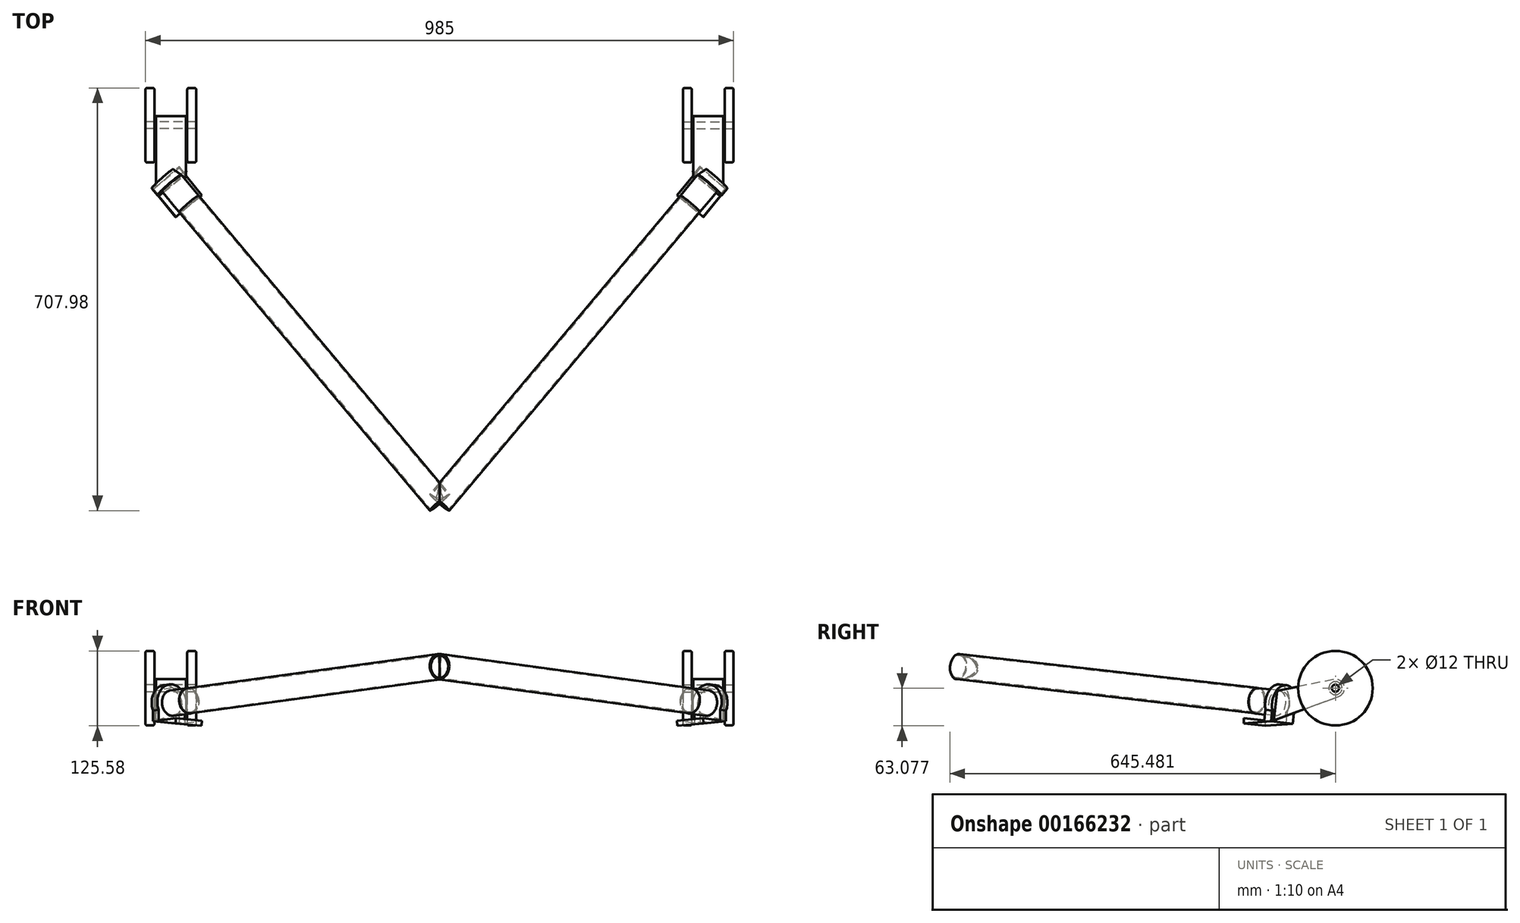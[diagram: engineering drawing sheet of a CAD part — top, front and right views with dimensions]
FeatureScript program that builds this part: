
annotation { "Feature Type Name" : "Feature", "Feature Type Description" : "" }
export const myFeature = defineFeature(function(context is Context, id is Id, definition is map)
    precondition{}
    {
        {
            var Q0;
            Q0=qCreatedBy(makeId("Top.planeOp"),FACE);
            var sketch = newSketch(context, id + "F0", { "sketchPlane" : qUnion([Q0])});
            skLineSegment(sketch, "E0", {"start": v(0, 492.45) * mm, "end": v(0, -616.45) * mm, "construction": true});
            skLineSegment(sketch, "E1", {"start": v(0, 0) * mm, "end": v(449.95, 536.23) * mm, "construction": true});
            skLineSegment(sketch, "E2", {"start": v(0, 0) * mm, "end": v(-449.95, 536.23) * mm, "construction": true});
            skSolve(sketch);
        }
        {
            var Q0;
            Q0=sQuery(id+"F0.wireOp",EDGE,"E1");
            var Q1;
            Q1=qCreatedBy(makeId("Front.planeOp"),FACE);
            cPlane(context, id + "F1", {"entities" : qUnion([Q0, Q1]), "cplaneType" : CPlaneType.LINE_ANGLE, "offset" : 25 * mm, "angle" : 0 * degree, "width" : 150 * mm, "height" : 150 * mm});
        }
        {
            var Q0;
            Q0=qCreatedBy(id+"F1.planeOp",FACE);
            var sketch = newSketch(context, id + "F2", { "sketchPlane" : qUnion([Q0])});
            skPoint(sketch, "E3.0", {"position": v(-700, 0) * mm});
            skLineSegment(sketch, "E4.0", {"start": v(0, 0) * mm, "end": v(-700, 0) * mm, "construction": true});
            skLineSegment(sketch, "E5", {"start": v(-700, 0) * mm, "end": v(0, 61.24) * mm, "construction": true});
            skSolve(sketch);
        }
        {
            var Q0;
            Q0=sQuery(id+"F2.wireOp",VERTEX,"E5.end");
            var Q1;
            Q1=sQuery(id+"F2.wireOp",EDGE,"E5");
            cPlane(context, id + "F3", {"entities" : qUnion([Q0, Q1]), "cplaneType" : CPlaneType.LINE_POINT, "offset" : 25 * mm, "width" : 150 * mm, "height" : 150 * mm});
        }
        {
            var Q0;
            Q0=qCreatedBy(id+"F3.planeOp",FACE);
            var sketch = newSketch(context, id + "F4", { "sketchPlane" : qUnion([Q0])});
            skPoint(sketch, "E6.0", {"position": v(4.45, 60.85) * mm});
            skCircle(sketch, "E7", {"center": v(4.45, 60.85) * mm, "radius": 21.3 * mm});
            skCircle(sketch, "E8.0", {"center": v(4.45, 60.85) * mm, "radius": 19.3 * mm});
            skSolve(sketch);
        }
        {
            var Q0;
            Q0 = qSketchRegion(id + "F4", true);
            extrude(context, id + "F5", {"entities" : qUnion([Q0]), "oppositeDirection" : true, "depth" : 700 * mm});
        }
        {
            var Q0;
            Q0=makeQuery(id+"F5.opExtrude","CAP_FACE",FACE,{"disambiguationData":[OSD([sQuery(id+"F4.wireOp",EDGE,"E7"),sQuery(id+"F4.wireOp",EDGE,"E8.0")])],"isStart":false});
            cPlane(context, id + "F6", {"entities" : qUnion([Q0]), "cplaneType" : CPlaneType.OFFSET, "offset" : (0.2 + 15) * mm, "width" : 150 * mm, "height" : 150 * mm});
        }
        {
            var Q0;
            Q0=qCreatedBy(id+"F6.planeOp",FACE);
            var sketch = newSketch(context, id + "F7", { "sketchPlane" : qUnion([Q0])});
            skCircle(sketch, "E9.0", {"center": v(-4.45, 60.85) * mm, "radius": 21.45 * mm});
            skArc(sketch, "E10.0", {"start": v(23.98, 47.4) * mm, "mid": v(-4.45, 92.3) * mm, "end": v(-32.88, 47.4) * mm});
            skLineSegment(sketch, "E11.top", {"start": v(-32.88, 29.4) * mm, "end": v(23.98, 29.4) * mm});
            skLineSegment(sketch, "E11.left", {"start": v(-32.88, 47.4) * mm, "end": v(-32.88, 29.4) * mm});
            skLineSegment(sketch, "E11.right", {"start": v(23.98, 47.4) * mm, "end": v(23.98, 29.4) * mm});
            skPoint(sketch, "E12", {"position": v(-4.45, 29.4) * mm});
            skSolve(sketch);
        }
        {
            var Q0;
            Q0=makeQuery(id+"F7.imprint","IMPRINT",FACE,{"disambiguationData":[TD([[makeQuery(id+"F7.imprint","IMPRINT",EDGE,{"derivedFrom":sQuery(id+"F7.wireOp",EDGE,"E9.0")}),-1.0]])]});
            var Q1;
            Q1=makeQuery(id+"F7.imprint","IMPRINT",FACE,{"disambiguationData":[TD([[makeQuery(id+"F7.imprint","IMPRINT",EDGE,{"derivedFrom":sQuery(id+"F7.wireOp",EDGE,"E9.0")}),1.0]])]});
            extrude(context, id + "F8", {"entities" : qUnion([Q0, Q1]), "oppositeDirection" : true, "depth" : 60 * mm});
        }
        {
            var Q0;
            Q0=makeQuery(id+"F8.opExtrude","CAP_FACE",FACE,{"disambiguationData":[OSD([sQuery(id+"F7.wireOp",EDGE,"E10.0"),sQuery(id+"F7.wireOp",EDGE,"E11.top"),sQuery(id+"F7.wireOp",EDGE,"E11.left"),sQuery(id+"F7.wireOp",EDGE,"E11.right")])],"isStart":false});
            var sketch = newSketch(context, id + "F9", { "sketchPlane" : qUnion([Q0])});
            skCircle(sketch, "E13.0", {"center": v(4.45, 60.85) * mm, "radius": 21.45 * mm});
            skSolve(sketch);
        }
        {
            var Q0;
            Q0=qCreatedBy(makeId("Right.planeOp"),FACE);
            cPlane(context, id + "F10", {"entities" : qUnion([Q0]), "cplaneType" : CPlaneType.OFFSET, "offset" : 475 * mm, "width" : 150 * mm, "height" : 150 * mm});
        }
        {
            var Q0;
            Q0=qCreatedBy(id+"F10.planeOp",FACE);
            var sketch = newSketch(context, id + "F11", { "sketchPlane" : qUnion([Q0])});
            skLineSegment(sketch, "E14.0", {"start": v(526.18, -12.39) * mm, "end": v(524.13, -30.27) * mm});
            skLineSegment(sketch, "E15", {"start": v(524.13, -30.27) * mm, "end": v(636.87, 11.03) * mm});
            skLineSegment(sketch, "E16", {"start": v(628.72, 39.82) * mm, "end": v(529.85, 19.73) * mm});
            skPoint(sketch, "E17.visualSharp", {"position": v(823.37, 79.36) * mm});
            skArc(sketch, "E17.filletArc", {"start": v(636.87, 11.03) * mm, "mid": v(646.14, 29.2) * mm, "end": v(628.72, 39.82) * mm});
            skCircle(sketch, "E18", {"center": v(631.71, 25.12) * mm, "radius": 6 * mm});
            skLineSegment(sketch, "E19", {"start": v(526.18, -12.39) * mm, "end": v(529.85, 19.73) * mm});
            skSolve(sketch);
        }
        {
            var Q0;
            Q0 = qSketchRegion(id + "F11", true);
            var Q1;
            {var subQ0=sQuery(id+"F7.wireOp",EDGE,"E9.0");Q1=makeQuery(id+"F5WumAtOTFpTSAU_2.boolean.opBoolean","MERGE",FACE,{"derivedFrom":[makeQuery(id+"F8.opExtrude","CAP_FACE",FACE,{"disambiguationData":[OSD([subQ0,sQuery(id+"F7.wireOp",EDGE,"E10.0"),sQuery(id+"F7.wireOp",EDGE,"E11.top"),sQuery(id+"F7.wireOp",EDGE,"E11.left"),sQuery(id+"F7.wireOp",EDGE,"E11.right")])],"isStart":true}),makeQuery(id+"F5WumAtOTFpTSAU_2.opExtrude","CAP_FACE",FACE,{"disambiguationData":[OSD([subQ0])],"isStart":true})]});}
            extrude(context, id + "F12", {"entities" : qUnion([Q0]), "operationType" : NewBodyOperationType.ADD, "oppositeDirection" : true, "endBoundEntityFace" : qUnion([Q1]), "depth" : 50 * mm});
        }
        {
            var Q0;
            Q0=makeQuery(id+"F12.opExtrude","CAP_FACE",FACE,{"disambiguationData":[OSD([sQuery(id+"F11.wireOp",EDGE,"E14.0"),sQuery(id+"F11.wireOp",EDGE,"E15"),sQuery(id+"F11.wireOp",EDGE,"E16"),sQuery(id+"F11.wireOp",EDGE,"E17.filletArc"),sQuery(id+"F11.wireOp",EDGE,"E18"),sQuery(id+"F11.wireOp",EDGE,"E19")])],"isStart":true});
            var Q1;
            {var subQ0=sQuery(id+"F11.wireOp",EDGE,"E17.filletArc");var subQ1=sQuery(id+"F11.wireOp",EDGE,"E16");var subQ2=sQuery(id+"F11.wireOp",EDGE,"E15");var subQ3=sQuery(id+"F11.wireOp",EDGE,"E18");Q1=makeQuery(id+"F12.boolean.opBoolean","SPLIT",FACE,{"disambiguationData":[TD([makeQuery(id+"F8.opExtrude","SWEPT_FACE",FACE,{"disambiguationData":[OSD([sQuery(id+"F7.wireOp",EDGE,"E10.0")])]})])],"derivedFrom":makeQuery(id+"F12.opExtrude","CAP_FACE",FACE,{"disambiguationData":[OSD([sQuery(id+"F11.wireOp",EDGE,"E14.0"),subQ2,subQ1,subQ0,subQ3,sQuery(id+"F11.wireOp",EDGE,"E19")])],"isStart":false})});}
            cPlane(context, id + "F13", {"entities" : qUnion([Q0, Q1]), "cplaneType" : CPlaneType.MID_PLANE, "offset" : 25 * mm, "width" : 150 * mm, "height" : 150 * mm});
        }
        {
            var Q0;
            Q0=qCreatedBy(id+"F13.planeOp",FACE);
            var sketch = newSketch(context, id + "F14", { "sketchPlane" : qUnion([Q0])});
            skCircle(sketch, "E20.0", {"center": v(631.71, 25.12) * mm, "radius": 6 * mm});
            skCircle(sketch, "E21.0", {"center": v(631.71, 25.12) * mm, "radius": 11 * mm});
            skSolve(sketch);
        }
        {
            var Q0;
            Q0 = qSketchRegion(id + "F14", true);
            extrude(context, id + "F15", {"entities" : qUnion([Q0]), "operationType" : NewBodyOperationType.ADD, "endBound" : BoundingType.SYMMETRIC, "depth" : 55 * mm});
        }
        {
            var Q0;
            Q0=makeQuery(id+"F15.opExtrude","CAP_FACE",FACE,{"disambiguationData":[OSD([sQuery(id+"F14.wireOp",EDGE,"E20.0"),sQuery(id+"F14.wireOp",EDGE,"E21.0")])],"isStart":true});
            var sketch = newSketch(context, id + "F16", { "sketchPlane" : qUnion([Q0])});
            skCircle(sketch, "E22", {"center": v(-631.71, 25.12) * mm, "radius": 62.5 * mm});
            skCircle(sketch, "E23.0", {"center": v(-631.71, 25.12) * mm, "radius": 6 * mm});
            skSolve(sketch);
        }
        {
            var Q0;
            Q0 = qSketchRegion(id + "F16", true);
            extrude(context, id + "F17", {"entities" : qUnion([Q0]), "depth" : 15 * mm});
        }
        {
            var Q0;
            Q0=makeQuery(id+"F17.opExtrude","CAP_EDGE",EDGE,{"disambiguationData":[OSD([sQuery(id+"F16.wireOp",EDGE,"E22")])],"isStart":false});
            var Q1;
            Q1=makeQuery(id+"F17.opExtrude","CAP_EDGE",EDGE,{"disambiguationData":[OSD([sQuery(id+"F16.wireOp",EDGE,"E22")])],"isStart":true});
            fillet(context, id + "F18", {"entities" : qUnion([Q0, Q1]), "radius" : 3 * mm, "tangentPropagation" : true, "allowEdgeOverflow" : false});
        }
        {
            var Q0;
            Q0=makeQuery(id+"F9.imprint","IMPRINT",FACE,{"disambiguationData":[TD([[makeQuery(id+"F9.imprint","IMPRINT",EDGE,{"derivedFrom":sQuery(id+"F9.wireOp",EDGE,"E13.0")}),-1.0]])]});
            extrude(context, id + "F19", {"entities" : qUnion([Q0]), "operationType" : NewBodyOperationType.REMOVE, "oppositeDirection" : true, "depth" : 45 * mm});
        }
        {
            var Q0;
            Q0=makeQuery(id+"F17.opExtrude","SWEPT_BODY",BODY,{"disambiguationData":[OSD([sQuery(id+"F16.wireOp",EDGE,"E22"),sQuery(id+"F16.wireOp",EDGE,"d09ed949-74d7-4649-ba00-194f00d450e0.0")])]});
            var Q1;
            Q1=makeQuery(id+"F12.opExtrude","SWEPT_FACE",FACE,{"disambiguationData":[OSD([sQuery(id+"F11.wireOp",EDGE,"E18")])]});
            transform(context, id + "F20", {"entities" : qUnion([Q0]), "transformType" : TransformType.TRANSLATION_DISTANCE, "transformDirection" : qUnion([Q1]), "distance" : (55 + 15) * mm, "oppositeDirection" : true, "makeCopy" : true});
        }
        {
            var Q0;
            Q0=makeQuery(id+"F8.opExtrude","SWEPT_FACE",FACE,{"disambiguationData":[OSD([sQuery(id+"F7.wireOp",EDGE,"E11.left")])]});
            var sketch = newSketch(context, id + "F21", { "sketchPlane" : qUnion([Q0])});
            skLineSegment(sketch, "E24.0", {"start": v(647.12, -66.5) * mm, "end": v(706.47, -75.33) * mm});
            skLineSegment(sketch, "E25", {"start": v(647.12, -75.33) * mm, "end": v(706.47, -75.33) * mm});
            skLineSegment(sketch, "E26", {"start": v(647.12, -66.5) * mm, "end": v(647.12, -75.33) * mm});
            skSolve(sketch);
        }
        {
            var Q0;
            Q0=makeQuery(id+"F21.imprint","IMPRINT",FACE,{"disambiguationData":[TD([[makeQuery(id+"F21.imprint","IMPRINT",EDGE,{"derivedFrom":sQuery(id+"F21.wireOp",EDGE,"E24.0")}),-1.0]])]});
            var Q1;
            Q1=makeQuery(id+"F8.opExtrude","SWEPT_FACE",FACE,{"disambiguationData":[OSD([sQuery(id+"F7.wireOp",EDGE,"E11.right")])]});
            extrude(context, id + "F22", {"entities" : qUnion([Q0]), "operationType" : NewBodyOperationType.ADD, "endBound" : BoundingType.UP_TO_SURFACE, "oppositeDirection" : true, "endBoundEntityFace" : qUnion([Q1]), "depth" : 25 * mm});
        }
        {
            var Q0;
            Q0=makeQuery(id+"F8.opExtrude","SWEPT_BODY",BODY,{"disambiguationData":[OSD([sQuery(id+"F7.wireOp",EDGE,"E9.0"),sQuery(id+"F7.wireOp",EDGE,"E10.0"),sQuery(id+"F7.wireOp",EDGE,"E11.top"),sQuery(id+"F7.wireOp",EDGE,"E11.left"),sQuery(id+"F7.wireOp",EDGE,"E11.right")])]});
            var Q1;
            Q1=makeQuery(id+"F5.opExtrude","SWEPT_BODY",BODY,{"disambiguationData":[OSD([sQuery(id+"F4.wireOp",EDGE,"E7"),sQuery(id+"F4.wireOp",EDGE,"E8.0")])]});
            var Q2;
            Q2=makeQuery(id+"F20.opPattern","COPY",BODY,{"derivedFrom":makeQuery(id+"F17.opExtrude","SWEPT_BODY",BODY,{"disambiguationData":[OSD([sQuery(id+"F16.wireOp",EDGE,"E22"),sQuery(id+"F16.wireOp",EDGE,"d09ed949-74d7-4649-ba00-194f00d450e0.0")])]}),"instanceName":"1"});
            var Q3;
            Q3=makeQuery(id+"F17.opExtrude","SWEPT_BODY",BODY,{"disambiguationData":[OSD([sQuery(id+"F16.wireOp",EDGE,"E22"),sQuery(id+"F16.wireOp",EDGE,"d09ed949-74d7-4649-ba00-194f00d450e0.0")])]});
            var Q4;
            Q4=qCreatedBy(makeId("Right.planeOp"),FACE);
            mirror(context, id + "F23", {"operationType" : NewBodyOperationType.ADD, "entities" : qUnion([Q0, Q1, Q2, Q3]), "mirrorPlane" : qUnion([Q4])});
        }
    });
